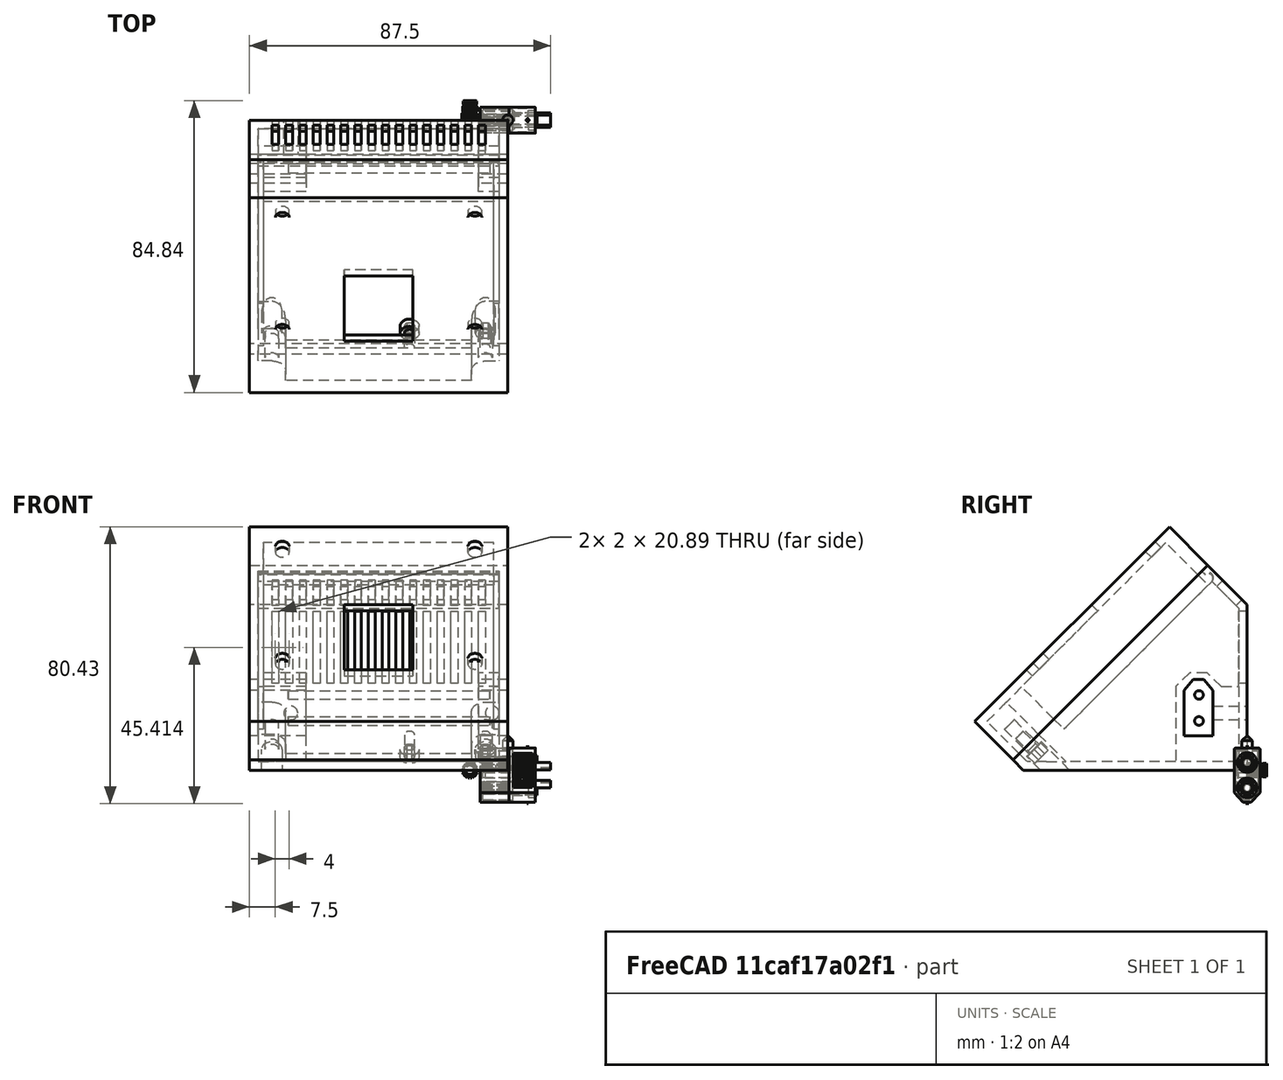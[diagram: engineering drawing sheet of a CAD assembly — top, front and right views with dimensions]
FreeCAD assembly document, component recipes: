
FREECAD ASSEMBLY — COMPONENT RECIPES ("moduleLidl_001_surBase35mm_009.1")

This assembly document has 8 components, labeled P0..P7 below (a component is one placed body or linked part). 4 of them carry a construction recipe — the FreeCAD feature program that regenerates the part from scratch, quoted from this document or its linked companion documents; the rest are supplied as boundary geometry only. No exploded tour is included for this assembly.
COMPONENT P0 — geometry summary ("adapt"; no construction recipe available for this part):
  bounding box: 65.0 x 49.5 x 49.5 mm
  tessellated surface: 2,488 triangles
  volume: 18576 mm^3 (12% of its bounding box)
  symmetry: mirror-symmetric across its x mid-plane
COMPONENT P1 — geometry summary ("fuse"; no construction recipe available for this part):
  bounding box: 31.7 x 29.8 x 15.0 mm
  tessellated surface: 6,264 triangles
  volume: 2885 mm^3 (20% of its bounding box)
  symmetry: mirror-symmetric across its x mid-plane
COMPONENT P2 — recipe-attached ("tigeLaiton001", modeled in this document).
Construction recipe (the document's own serialized feature program — sketch geometry with constraints, then the solid features built on it; lengths are millimeters unless a unit is written):

FEATURE [PartDesign::Plane] DatumPlane012  label="planBaseTige"
  AttachmentOffset = pos=(0,0,-5.18) rot=(0,0,1;0rad)
  Length = 60
  MapMode = 5
  Placement = pos=(-5.18,1.2e-15,-1.2e-15) rot=(0.57735,0.57735,0.57735;2.0944rad)
  ResizeMode = 0
  Support = -> [YZ_Plane012]
  Width = 60
  expr: .AttachmentOffset.Base.z = -<<tige>>.planBaseTigeposX
FEATURE [Sketcher::SketchObject] Sketch032  label="sk_tiges"
  FullyConstrained = true
  MapMode = 5
  Placement = pos=(-5.18,1.2e-15,-1.2e-15) rot=(0.57735,0.57735,0.57735;2.0944rad)
  Support = -> [DatumPlane012]
  expr: Constraints[0] = <<tige>>.tigeDiam
  expr: Constraints[1] = <<tige>>.tigePosY
  expr: Constraints[2] = <<tige>>.tigePosX
  sketch-geometry (1):
    g0: Circle CenterX=-14 CenterY=14.3 CenterZ=0 NormalX=0 NormalY=0 NormalZ=1 AngleXU=0 Radius=1.25
  constraints (3):
    c: Diameter(g0) = 2.5
    c: DistanceY(g-1,g0) = 14.3
    c: DistanceX(g0,g-1) = 14
FEATURE [PartDesign::Pad] Pad017  label="tigeBasse"
  AllowMultiFace = false
  Direction = (1,-1e-16,1e-16)
  Length = 58.62
  Length2 = 100
  Placement = pos=(-5.18,1e-15,-1e-15) rot=(0.57735,0.57735,0.57735;2.0944rad)
  Profile = -> Sketch032
  Reversed = true
  Type = 0
  expr: Length = <<tige>>.tigeLong
FEATURE [PartDesign::Body] Body007  label="tigeLaiton"
  Group = -> [DatumPlane012,Sketch032,Pad017]
  Origin = -> Origin016
  Tip = -> Pad017
FEATURE [PartDesign::Plane] DatumPlane013  label="planTige2"
  AttachmentOffset = pos=(0,0,-5.18) rot=(0,0,1;0rad)
  Length = 60
  MapMode = 5
  Placement = pos=(-5.18,1.2e-15,-1.2e-15) rot=(0.57735,0.57735,0.57735;2.0944rad)
  ResizeMode = 0
  Support = -> [YZ_Plane014]
  Width = 60
  expr: .AttachmentOffset.Base.z = -<<tige>>.planBaseTigeposX
FEATURE [Sketcher::SketchObject] Sketch033  label="sk_tige2"
  FullyConstrained = true
  MapMode = 5
  Placement = pos=(-5.18,1.2e-15,-1.2e-15) rot=(0.57735,0.57735,0.57735;2.0944rad)
  Support = -> [DatumPlane013]
  expr: Constraints[0] = <<tige>>.tigeDiam
  expr: Constraints[1] = <<tige>>.tigePosX
  expr: Constraints[2] = <<tige>>.tigePosY + <<tige>>.xtEcartBroches
  sketch-geometry (1):
    g0: Circle CenterX=-14 CenterY=21.86 CenterZ=0 NormalX=0 NormalY=0 NormalZ=1 AngleXU=0 Radius=1.25
  constraints (3):
    c: Diameter(g0) = 2.5
    c: DistanceX(g0,g-1) = 14
    c: DistanceY(g-1,g0) = 21.86
FEATURE [PartDesign::Pad] Pad018
  AllowMultiFace = false
  Direction = (1,-1e-16,1e-16)
  Length = 58.62
  Length2 = 100
  Placement = pos=(-5.18,1e-15,-1e-15) rot=(0.57735,0.57735,0.57735;2.0944rad)
  Profile = -> Sketch033
  Reversed = true
  Type = 0
  expr: Length = <<tige>>.tigeLong
FEATURE [PartDesign::Body] Body008  label="tige2"
  Group = -> [DatumPlane013,Sketch033,Pad018]
  Origin = -> Origin018
  Tip = -> Pad018
COMPONENT P3 — geometry summary ("xtVisInsertFix"; no construction recipe available for this part):
  bounding box: 20.2 x 17.7 x 16.6 mm
  tessellated surface: 21,322 triangles
  volume: 1306 mm^3 (22% of its bounding box)
COMPONENT P4 — recipe-attached ("visInsertFavFix", modeled in this document).
Construction recipe (the document's own serialized feature program — sketch geometry with constraints, then the solid features built on it; lengths are millimeters unless a unit is written):

FEATURE [Sketcher::SketchObject] Sketch034  label="Sketch"
  FullyConstrained = false
  MapMode = 5
  Support = -> [XY_Plane015]
  sketch-geometry (1):
    g0: Circle CenterX=0 CenterY=0 CenterZ=0 NormalX=0 NormalY=0 NormalZ=1 AngleXU=0 Radius=2.75
  constraints (2):
    c: Coincident(g0,g-1)
    c: Diameter(g0) = 5.5
FEATURE [PartDesign::Pad] Pad019  label="tete"
  AllowMultiFace = false
  Direction = (1,1,1)
  Length = 3
  Length2 = 100
  Profile = -> Sketch034
  Type = 0
FEATURE [Sketcher::SketchObject] Sketch001
  FullyConstrained = false
  MapMode = 5
  Placement = pos=(0,0,0) rot=(1,0,0;3.14159rad)
  Support = -> [Pad019]
  sketch-geometry (1):
    g0: Circle CenterX=0 CenterY=0 CenterZ=0 NormalX=0 NormalY=0 NormalZ=1 AngleXU=0 Radius=1.5
  constraints (2):
    c: Coincident(g0,g-1)
    c: Diameter(g0) = 3
FEATURE [PartDesign::Pad] Pad020  label="corps"
  AllowMultiFace = false
  BaseFeature = -> Pad019
  Direction = (1,1,1)
  Length = 6
  Length2 = 100
  Profile = -> Sketch001
  Type = 0
FEATURE [PartDesign::Plane] DatumPlane014
  AttachmentOffset = pos=(0,0,3) rot=(0,0,1;0rad)
  Length = 60
  MapMode = 5
  Placement = pos=(0,0,3) rot=(0,0,1;0rad)
  ResizeMode = 0
  Support = -> [XY_Plane015]
  Width = 60
FEATURE [Sketcher::SketchObject] Sketch035  label="Sketch002"
  FullyConstrained = false
  MapMode = 5
  Placement = pos=(0,0,3) rot=(0,0,1;0rad)
  Support = -> [DatumPlane014]
  sketch-geometry (7):
    g0: LineSegment StartX=0.721688 StartY=-1.25 StartZ=0 EndX=1.44338 EndY=1.0119e-12 EndZ=0
    g1: LineSegment StartX=1.44338 StartY=1.0119e-12 StartZ=0 EndX=0.721688 EndY=1.25 EndZ=0
    g2: LineSegment StartX=0.721688 StartY=1.25 StartZ=0 EndX=-0.721688 EndY=1.25 EndZ=0
    g3: LineSegment StartX=-0.721688 StartY=1.25 StartZ=0 EndX=-1.44338 EndY=8.689e-13 EndZ=0
    g4: LineSegment StartX=-1.44338 StartY=8.689e-13 StartZ=0 EndX=-0.721688 EndY=-1.25 EndZ=0
    g5: LineSegment StartX=-0.721688 StartY=-1.25 StartZ=0 EndX=0.721688 EndY=-1.25 EndZ=0
    g6: Circle CenterX=0 CenterY=0 CenterZ=0 NormalX=0 NormalY=0 NormalZ=1 AngleXU=0 Radius=1.44338
  constraints (16):
    c: Coincident(g0,g1)
    c: Coincident(g1,g2)
    c: Coincident(g2,g3)
    c: Coincident(g3,g4)
    c: Coincident(g4,g5)
    c: Coincident(g5,g0)
    c: Equal(g0, g1-g5) x5
    c: PointOnObject(g0,g6)
    c: PointOnObject(g1,g6)
    c: PointOnObject(g2,g6)
    c: PointOnObject(g3,g6)
    c: PointOnObject(g4,g6)
    c: PointOnObject(g5,g6)
    c: Coincident(g6,g-1)
    c: Horizontal(g2)
    c: DistanceY(g0,g1) = 2.5
FEATURE [PartDesign::Pocket] Pocket016  label="emprunte"
  AllowMultiFace = false
  BaseFeature = -> Pad020
  Direction = (1,1,1)
  Length = 4
  Length2 = 100
  Profile = -> Sketch035
  Type = 0
FEATURE [PartDesign::Body] Body009  label="visTHCM3x6_FAV001"
  Group = -> [Sketch034,Pad019,Sketch001,Pad020,DatumPlane014,Sketch035,Pocket016]
  Origin = -> Origin019
  Placement = pos=(-6.5,-61.8718,6.01041) rot=(1,0,0;3.92699rad)
  Tip = -> Pocket016
COMPONENT P5 — recipe-attached ("visInserFavMob", modeled in this document).
Construction recipe (the document's own serialized feature program — sketch geometry with constraints, then the solid features built on it; lengths are millimeters unless a unit is written):

FEATURE [Sketcher::SketchObject] Sketch036
  FullyConstrained = false
  MapMode = 5
  Support = -> [XY_Plane016]
  sketch-geometry (1):
    g0: Circle CenterX=0 CenterY=0 CenterZ=0 NormalX=0 NormalY=0 NormalZ=1 AngleXU=0 Radius=2.75
  constraints (2):
    c: Coincident(g0,g-1)
    c: Diameter(g0) = 5.5
FEATURE [PartDesign::Pad] Pad021  label="tete001"
  AllowMultiFace = false
  Direction = (1,1,1)
  Length = 3
  Length2 = 100
  Profile = -> Sketch036
  Type = 0
FEATURE [Sketcher::SketchObject] Sketch037
  FullyConstrained = false
  MapMode = 5
  Placement = pos=(0,0,0) rot=(1,0,0;3.14159rad)
  Support = -> [Pad021]
  sketch-geometry (1):
    g0: Circle CenterX=0 CenterY=0 CenterZ=0 NormalX=0 NormalY=0 NormalZ=1 AngleXU=0 Radius=1.5
  constraints (2):
    c: Coincident(g0,g-1)
    c: Diameter(g0) = 3
FEATURE [PartDesign::Pad] Pad022  label="corps001"
  AllowMultiFace = false
  BaseFeature = -> Pad021
  Direction = (1,1,1)
  Length = 6
  Length2 = 100
  Profile = -> Sketch037
  Type = 0
FEATURE [PartDesign::Plane] DatumPlane015
  AttachmentOffset = pos=(0,0,3) rot=(0,0,1;0rad)
  Length = 60
  MapMode = 5
  Placement = pos=(0,0,3) rot=(0,0,1;0rad)
  ResizeMode = 0
  Support = -> [XY_Plane016]
  Width = 60
FEATURE [Sketcher::SketchObject] Sketch038
  FullyConstrained = false
  MapMode = 5
  Placement = pos=(0,0,3) rot=(0,0,1;0rad)
  Support = -> [DatumPlane015]
  sketch-geometry (7):
    g0: LineSegment StartX=0.721688 StartY=-1.25 StartZ=0 EndX=1.44338 EndY=1.0119e-12 EndZ=0
    g1: LineSegment StartX=1.44338 StartY=1.0119e-12 StartZ=0 EndX=0.721688 EndY=1.25 EndZ=0
    g2: LineSegment StartX=0.721688 StartY=1.25 StartZ=0 EndX=-0.721688 EndY=1.25 EndZ=0
    g3: LineSegment StartX=-0.721688 StartY=1.25 StartZ=0 EndX=-1.44338 EndY=8.689e-13 EndZ=0
    g4: LineSegment StartX=-1.44338 StartY=8.689e-13 StartZ=0 EndX=-0.721688 EndY=-1.25 EndZ=0
    g5: LineSegment StartX=-0.721688 StartY=-1.25 StartZ=0 EndX=0.721688 EndY=-1.25 EndZ=0
    g6: Circle CenterX=0 CenterY=0 CenterZ=0 NormalX=0 NormalY=0 NormalZ=1 AngleXU=0 Radius=1.44338
  constraints (16):
    c: Coincident(g0,g1)
    c: Coincident(g1,g2)
    c: Coincident(g2,g3)
    c: Coincident(g3,g4)
    c: Coincident(g4,g5)
    c: Coincident(g5,g0)
    c: Equal(g0, g1-g5) x5
    c: PointOnObject(g0,g6)
    c: PointOnObject(g1,g6)
    c: PointOnObject(g2,g6)
    c: PointOnObject(g3,g6)
    c: PointOnObject(g4,g6)
    c: PointOnObject(g5,g6)
    c: Coincident(g6,g-1)
    c: Horizontal(g2)
    c: DistanceY(g0,g1) = 2.5
FEATURE [PartDesign::Pocket] Pocket017  label="emprunte001"
  AllowMultiFace = false
  BaseFeature = -> Pad022
  Direction = (1,1,1)
  Length = 4
  Length2 = 100
  Profile = -> Sketch038
  Type = 0
FEATURE [PartDesign::Body] Body010  label="visTHCM3x6_FAV002"
  Group = -> [Sketch036,Pad021,Sketch037,Pad022,DatumPlane015,Sketch038,Pocket017]
  Origin = -> Origin020
  Placement = pos=(-28.5,-61.8718,6.01041) rot=(1,0,0;3.92699rad)
  Tip = -> Pocket017
COMPONENT P6 — recipe-attached ("BaseModule", modeled in this document).
Construction recipe (the document's own serialized feature program — sketch geometry with constraints, then the solid features built on it; lengths are millimeters unless a unit is written):

FEATURE [PartDesign::FeatureBase] Clone
  BaseFeature = -> Slice_child0
FEATURE [PartDesign::FeatureBase] Clone001
  BaseFeature = -> Slice_child1
FEATURE [PartDesign::Thickness] Thickness
  Base = -> Clone [Face7]
  BaseFeature = -> Clone
  Intersection = false
  Join = 0
  Mode = 0
  Reversed = true
  SupportTransform = false
  Value = 2.5
  expr: Value = <<sp>>.epaisseurParois
FEATURE [PartDesign::Thickness] Thickness001
  Base = -> Clone001 [Face5]
  BaseFeature = -> Clone001
  Intersection = false
  Join = 0
  Mode = 0
  Reversed = true
  SupportTransform = false
  Value = 2.5
  expr: Value = <<sp>>.epaisseurParois
FEATURE [PartDesign::Plane] DatumPlane001  label="planXt"
  AttachmentOffset = pos=(0,0,-2.5) rot=(0,0,1;0rad)
  Length = 110.737
  MapMode = 5
  Placement = pos=(-2.5,6e-16,-6e-16) rot=(0.57735,0.57735,0.57735;2.0944rad)
  ResizeMode = 0
  Support = -> [YZ_Plane002]
  Width = 102.305
  expr: .AttachmentOffset.Base.z = -<<sp>>.epaisseurParois
FEATURE [Sketcher::SketchObject] Sketch002  label="sk_renfortXt"
  FullyConstrained = true
  MapMode = 5
  Placement = pos=(-2.5,6e-16,-6e-16) rot=(0.57735,0.57735,0.57735;2.0944rad)
  Support = -> [DatumPlane001]
  expr: .Constraints.dist = <<sp>>.xt60distanceAngleBord
  expr: .Constraints.epRf = <<sp>>.xt60epRenfort
  expr: Constraints[13] = <<sp>>.xt60largeurFetiere
  expr: Constraints[14] = <<sp>>.xt60hauteur
  expr: Constraints[15] = <<sp>>.xt60hauteurToit
  expr: Constraints[16] = <<sp>>.xt60base
  expr: Constraints[18] = .Constraints.dist
  expr: Constraints[31] = <<sp>>.epaisseurParois
  expr: Constraints[32] = .Constraints.epRf
  expr: Constraints[34] = .Constraints.epRf
  expr: Constraints[45] = <<sp>>.epaisseurParois
  sketch-geometry (17):
    g0: LineSegment StartX=-18.3 StartY=10 StartZ=0 EndX=-18.3 EndY=23.25 EndZ=0
    g1: LineSegment StartX=-18.3 StartY=23.25 StartZ=0 EndX=-15.65 EndY=25.75 EndZ=0
    g2: LineSegment StartX=-15.65 StartY=25.75 StartZ=0 EndX=-12.65 EndY=25.75 EndZ=0
    g3: LineSegment StartX=-12.65 StartY=25.75 StartZ=0 EndX=-10 EndY=23.25 EndZ=0
    g4: LineSegment StartX=-10 StartY=23.25 StartZ=0 EndX=-10 EndY=10 EndZ=0
    g5: LineSegment StartX=-10 StartY=10 StartZ=0 EndX=-18.3 EndY=10 EndZ=0
    g6: LineSegment StartX=-14.15 StartY=10 StartZ=0 EndX=-14.15 EndY=25.75 EndZ=0
    g7: LineSegment StartX=-16.6431 StartY=28.25 StartZ=0 EndX=-20.8 EndY=24.3284 EndZ=0
    g8: LineSegment StartX=-20.8 StartY=24.3284 StartZ=0 EndX=-20.8 EndY=2.5 EndZ=0
    g9: LineSegment StartX=-20.8 StartY=2.5 StartZ=0 EndX=-7.5 EndY=2.5 EndZ=0
    g10: LineSegment StartX=-7.5 StartY=2.5 StartZ=0 EndX=-7.5 EndY=24.3284 EndZ=0
    g11: LineSegment StartX=-7.5 StartY=24.3284 StartZ=0 EndX=-11.6569 EndY=28.25 EndZ=0
    g12: LineSegment StartX=-11.6569 StartY=28.25 StartZ=0 EndX=-16.6431 EndY=28.25 EndZ=0
    g13: LineSegment StartX=-7.5 StartY=24.3284 StartZ=0 EndX=-2.5 EndY=24.3284 EndZ=0
    g14: LineSegment StartX=-2.5 StartY=24.3284 StartZ=0 EndX=-2.5 EndY=2.5 EndZ=0
    g15: LineSegment StartX=-2.5 StartY=2.5 StartZ=0 EndX=-7.5 EndY=2.5 EndZ=0
    g16: LineSegment StartX=-7.5 StartY=2.5 StartZ=0 EndX=-7.5 EndY=24.3284 EndZ=0
  constraints (46):
    c: Vertical(g0)
    c: Coincident(g0,g1)
    c: Coincident(g1,g2)
    c: Horizontal(g2)
    c: Coincident(g2,g3)
    c: Coincident(g3,g4)
    c: Vertical(g4)
    c: Coincident(g4,g5)
    c: Coincident(g5,g0)
    c: Horizontal(g5)
    c: Symmetric(g1,g2,g6)
    c: Equal(g0,g4)
    c: Symmetric(g0,g4,g6)
    c: DistanceX(g2,g2) = 3
    c: DistanceY(g4,g4) = 13.25
    c: DistanceY(g3,g2) = 2.5
    c: DistanceX(g5,g5) = 8.3
    c: DistanceX(g4,g-1) = 10  'dist'
    c: DistanceY(g-1,g4) = 10
    c: Coincident(g7,g8)
    c: Vertical(g8)
    c: Coincident(g8,g9)
    c: Horizontal(g9)
    c: Coincident(g9,g10)
    c: Coincident(g10,g11)
    c: Coincident(g11,g12)
    c: Coincident(g12,g7)
    c: Symmetric(g7,g10,g6)
    c: Symmetric(g7,g11,g6)
    c: Symmetric(g8,g9,g6)
    c: DistanceX(g8,g0) = 2.5  'epRf'
    c: DistanceY(g-1,g9) = 2.5
    c: Distance(g7,g1) = 2.5
    c: Parallel(g1,g7)
    c: DistanceY(g2,g11) = 2.5
    c: Coincident(g13,g14)
    c: Coincident(g14,g15)
    c: Coincident(g15,g16)
    c: Coincident(g16,g13)
    c: Horizontal(g13)
    c: Horizontal(g15)
    c: Vertical(g14)
    c: Vertical(g16)
    c: Coincident(g13,g11)
    c: Horizontal(g14,g9)
    c: DistanceX(g14,g-1) = 2.5
FEATURE [PartDesign::Pad] Pad001  label="renfortXt"
  AllowMultiFace = false
  BaseFeature = -> Thickness
  Direction = (1,-1e-16,1e-16)
  Length = 70
  Length2 = 100
  Profile = -> Sketch002
  Reversed = true
  Type = 0
  expr: Length = <<sp>>.largeurModuleBase - 2 * <<sp>>.epaisseurParois
FEATURE [Sketcher::SketchObject] Sketch003  label="sk_trouXt"
  FullyConstrained = true
  MapMode = 5
  Placement = pos=(0,0,0) rot=(0.57735,0.57735,0.57735;2.0944rad)
  Support = -> [YZ_Plane002]
  expr: .Constraints.dist = <<sp>>.xt60distanceAngleBord
  expr: Constraints[13] = <<sp>>.xt60base
  expr: Constraints[14] = <<sp>>.xt60hauteur
  expr: Constraints[15] = <<sp>>.xt60hauteurToit + <<sp>>.xtJeu
  expr: Constraints[16] = <<sp>>.xt60largeurFetiere
  expr: Constraints[18] = .Constraints.dist
  sketch-geometry (7):
    g0: LineSegment StartX=-18.3 StartY=10 StartZ=0 EndX=-18.3 EndY=23.25 EndZ=0
    g1: LineSegment StartX=-18.3 StartY=23.25 StartZ=0 EndX=-15.65 EndY=26.35 EndZ=0
    g2: LineSegment StartX=-15.65 StartY=26.35 StartZ=0 EndX=-12.65 EndY=26.35 EndZ=0
    g3: LineSegment StartX=-12.65 StartY=26.35 StartZ=0 EndX=-10 EndY=23.25 EndZ=0
    g4: LineSegment StartX=-10 StartY=23.25 StartZ=0 EndX=-10 EndY=10 EndZ=0
    g5: LineSegment StartX=-10 StartY=10 StartZ=0 EndX=-18.3 EndY=10 EndZ=0
    g6: LineSegment StartX=-14.15 StartY=10 StartZ=0 EndX=-14.15 EndY=26.35 EndZ=0
  constraints (19):
    c: Vertical(g0)
    c: Coincident(g0,g1)
    c: Coincident(g1,g2)
    c: Horizontal(g2)
    c: Coincident(g2,g3)
    c: Coincident(g3,g4)
    c: Coincident(g4,g5)
    c: Coincident(g5,g0)
    c: Horizontal(g5)
    c: Symmetric(g1,g2,g6)
    c: Symmetric(g0,g3,g6)
    c: Vertical(g6)
    c: Symmetric(g0,g4,g6)
    c: DistanceX(g5,g5) = 8.3
    c: DistanceY(g4,g4) = 13.25
    c: DistanceY(g3,g2) = 3.1
    c: DistanceX(g2,g2) = 3
    c: DistanceX(g4,g-1) = 10  'dist'
    c: DistanceY(g-1,g4) = 10
FEATURE [PartDesign::Pocket] Pocket
  AllowMultiFace = false
  BaseFeature = -> Pad001
  Direction = (-1,2e-16,-3e-16)
  Length = 75
  Length2 = 100
  Profile = -> Sketch003
  Type = 0
  expr: Length = <<sp>>.largeurModuleBase
FEATURE [PartDesign::Plane] DatumPlane002  label="planDecoupeRenfortXt"
  AttachmentOffset = pos=(0,0,2.5) rot=(0,0,1;0rad)
  Length = 118.392
  MapMode = 5
  Placement = pos=(0,-2.5,-6e-16) rot=(1,0,0;1.5708rad)
  ResizeMode = 0
  Support = -> [XZ_Plane002]
  Width = 102.961
  expr: .AttachmentOffset.Base.z = <<sp>>.epaisseurParois
FEATURE [Sketcher::SketchObject] Sketch004  label="sk_decoupRenfXt"
  FullyConstrained = true
  MapMode = 5
  Placement = pos=(0,-2.5,-6e-16) rot=(1,0,0;1.5708rad)
  Support = -> [DatumPlane002]
  expr: Constraints[10] = <<sp>>.xt60LongueurRenfortPetit + <<sp>>.epaisseurParois
  expr: Constraints[11] = <<sp>>.largeurModuleBase - (<<sp>>.xt60longueurRenfortGrand + <<sp>>.epaisseurParois)
  expr: Constraints[8] = <<sp>>.epaisseurParois
  expr: Constraints[9] = <<sp>>.xt60distanceAngleBord + <<sp>>.xt60hauteur + <<sp>>.xt60hauteurToit + <<sp>>.xt60epRenfort
  sketch-geometry (4):
    g0: LineSegment StartX=-58.5 StartY=28.25 StartZ=0 EndX=-8.5 EndY=28.25 EndZ=0
    g1: LineSegment StartX=-8.5 StartY=28.25 StartZ=0 EndX=-8.5 EndY=2.5 EndZ=0
    g2: LineSegment StartX=-8.5 StartY=2.5 StartZ=0 EndX=-58.5 EndY=2.5 EndZ=0
    g3: LineSegment StartX=-58.5 StartY=2.5 StartZ=0 EndX=-58.5 EndY=28.25 EndZ=0
  constraints (12):
    c: Coincident(g0,g1)
    c: Coincident(g1,g2)
    c: Coincident(g2,g3)
    c: Coincident(g3,g0)
    c: Horizontal(g0)
    c: Horizontal(g2)
    c: Vertical(g1)
    c: Vertical(g3)
    c: DistanceY(g-1,g1) = 2.5
    c: DistanceY(g-1,g0) = 28.25
    c: DistanceX(g1,g-1) = 8.5
    c: DistanceX(g2,g-1) = 58.5
FEATURE [PartDesign::Pocket] Pocket001  label="decoupeRenfXt"
  AllowMultiFace = false
  BaseFeature = -> Pocket
  Direction = (0,1,2e-16)
  Length = 23.3
  Length2 = 100
  Profile = -> Sketch004
  Reversed = true
  Type = 0
  expr: Length = <<sp>>.xt60distanceAngleBord + <<sp>>.xt60base + 2 * <<sp>>.xt60epRenfort
FEATURE [Sketcher::SketchObject] Sketch005  label="xt60PercagePostMale"
  FullyConstrained = true
  MapMode = 5
  Placement = pos=(0,0,0) rot=(1,0,0;1.5708rad)
  Support = -> [XZ_Plane002]
  expr: Constraints[0] = <<sp>>.insertDiamPercage
  expr: Constraints[1] = <<sp>>.insertDistanceTrouBordMale
  expr: Constraints[2] = <<sp>>.insertHauteur
  sketch-geometry (1):
    g0: Circle CenterX=-4.5 CenterY=16.625 CenterZ=0 NormalX=0 NormalY=0 NormalZ=1 AngleXU=0 Radius=2
  constraints (3):
    c: Diameter(g0) = 4
    c: DistanceX(g0,g-1) = 4.5
    c: DistanceY(g-1,g0) = 16.625
FEATURE [PartDesign::Pocket] Pocket002  label="insertXtMale"
  AllowMultiFace = false
  BaseFeature = -> Pocket001
  Direction = (0,1,2e-16)
  Length = 10
  Length2 = 100
  Profile = -> Sketch005
  Reversed = true
  Type = 0
  expr: Length = <<sp>>.insertProfondeurPercage
FEATURE [Sketcher::SketchObject] Sketch006  label="xt60PercagePostFem"
  FullyConstrained = true
  MapMode = 5
  Placement = pos=(0,0,0) rot=(1,0,0;1.5708rad)
  Support = -> [XZ_Plane002]
  expr: Constraints[0] = <<sp>>.insertDiamPercage
  expr: Constraints[1] = <<sp>>.insertDistanceTrouBordFem
  expr: Constraints[2] = <<sp>>.insertHauteur
  sketch-geometry (1):
    g0: Circle CenterX=-63 CenterY=16.625 CenterZ=0 NormalX=0 NormalY=0 NormalZ=1 AngleXU=0 Radius=2
  constraints (3):
    c: Diameter(g0) = 4
    c: DistanceX(g0,g-1) = 63
    c: DistanceY(g-1,g0) = 16.625
FEATURE [PartDesign::Pocket] Pocket003  label="insertXt60Fem"
  AllowMultiFace = false
  BaseFeature = -> Pocket002
  Direction = (0,1,2e-16)
  Length = 10
  Length2 = 100
  Profile = -> Sketch006
  Reversed = true
  Type = 0
  expr: Length = <<sp>>.insertProfondeurPercage
FEATURE [PartDesign::Plane] DatumPlane003
  AttachmentOffset = pos=(0,0,2.5) rot=(0,0,1;0rad)
  Length = 119.287
  MapMode = 2
  Placement = pos=(0,0,2.5) rot=(0,0,1;0rad)
  ResizeMode = 0
  Support = -> [XY_Plane002]
  Width = 112.287
  expr: .AttachmentOffset.Base.z = <<sp>>.epaisseurParois
FEATURE [PartDesign::Plane] DatumPlane004  label="planTrancheur"
  AttachmentOffset = pos=(0,0,71) rot=(-1,0,0;0.785398rad)
  Length = 122.411
  MapMode = 5
  Placement = pos=(0,-71,-1.58e-14) rot=(1,0,0;0.785398rad)
  ResizeMode = 0
  Support = -> [XZ_Plane002]
  Width = 147.971
  expr: .AttachmentOffset.Base.z = <<sp>>.planTrancheur
FEATURE [Sketcher::SketchObject] Sketch008
  FullyConstrained = true
  MapMode = 5
  Placement = pos=(0,-71,-2.13e-14) rot=(1,0,0;0.785398rad)
  Support = -> [DatumPlane004]
  expr: .Constraints.dist = <<sp>>.epaisseurParois
  expr: Constraints[13] = <<sp>>.epaisseurParois
  expr: Constraints[16] = <<sp>>.insertDiamPercage / 2 + <<sp>>.insertFAVMargeDist
  expr: Constraints[1] = <<sp>>.insertFavDistAuZeroDuPLan
  expr: Constraints[21] = <<sp>>.insertFAVDistBord
  expr: Constraints[22] = <<sp>>.largeurModuleBase - <<sp>>.epaisseurParois
  sketch-geometry (7):
    g0: LineSegment StartX=-2.5 StartY=4.24264 StartZ=0 EndX=-72.5 EndY=4.24264 EndZ=0
    g1: LineSegment StartX=-6.5 StartY=14.7426 StartZ=0 EndX=-2.5 EndY=14.7426 EndZ=0
    g2: LineSegment StartX=-2.5 StartY=14.7426 StartZ=0 EndX=-2.5 EndY=6.74264 EndZ=0
    g3: LineSegment StartX=-2.5 StartY=6.74264 StartZ=0 EndX=-10.5 EndY=6.74264 EndZ=0
    g4: LineSegment StartX=-10.5 StartY=6.74264 StartZ=0 EndX=-10.5 EndY=10.7426 EndZ=0
    g5: ArcOfCircle CenterX=-6.5 CenterY=10.7426 CenterZ=0 NormalX=0 NormalY=0 NormalZ=1 AngleXU=0 Radius=4 StartAngle=1.5708 EndAngle=3.14159
    g6: LineSegment StartX=-6.5 StartY=10.7426 StartZ=0 EndX=-6.5 EndY=6.74264 EndZ=0
  constraints (23):
    c: Horizontal(g0)
    c: DistanceY(g-1,g0) = 4.24264
    c: DistanceX(g0,g-1) = 2.5  'dist'
    c: Horizontal(g1)
    c: Coincident(g1,g2)
    c: Vertical(g2)
    c: Coincident(g2,g3)
    c: Horizontal(g3)
    c: Coincident(g3,g4)
    c: Vertical(g4)
    c: Vertical(g2,g0)
    c: Equal(g3,g2)
    c: Equal(g4,g1)
    c: DistanceY(g0,g2) = 2.5
    c: Coincident(g5,g4)
    c: Coincident(g5,g1)
    c: DistanceX(g5,g2) = 4
    c: Coincident(g6,g5)
    c: PointOnObject(g6,g3)
    c: Vertical(g6)
    c: Vertical(g5,g1)
    c: DistanceX(g3,g3) = 8
    c: DistanceX(g0,g-1) = 72.5
FEATURE [PartDesign::Pad] Pad003  label="padTrouFAVDroite"
  AllowMultiFace = false
  BaseFeature = -> Pocket003
  Direction = (0,-0.707107,0.707107)
  Length = 10
  Length2 = 100
  Profile = -> Sketch008
  Reversed = true
  Type = 3
  UpToFace = -> DatumPlane003
FEATURE [Sketcher::SketchObject] Sketch009
  FullyConstrained = true
  MapMode = 5
  Placement = pos=(0,-71,-2.13e-14) rot=(1,0,0;0.785398rad)
  Support = -> [DatumPlane004]
  expr: .Constraints.larg = <<sp>>.insertFAVDistBord
  expr: Constraints[11] = .Constraints.larg / 2
  expr: Constraints[12] = <<sp>>.largeurModuleBase
  expr: Constraints[13] = <<sp>>.insertFavDistAuZeroDuPLan
  expr: Constraints[14] = <<sp>>.epaisseurParois
  expr: Constraints[15] = <<sp>>.epaisseurParois
  expr: Constraints[8] = .Constraints.larg
  sketch-geometry (6):
    g0: LineSegment StartX=-72.5 StartY=6.74264 StartZ=0 EndX=-64.5 EndY=6.74264 EndZ=0
    g1: LineSegment StartX=-64.5 StartY=6.74264 StartZ=0 EndX=-64.5 EndY=10.7426 EndZ=0
    g2: LineSegment StartX=-68.5 StartY=14.7426 StartZ=0 EndX=-72.5 EndY=14.7426 EndZ=0
    g3: LineSegment StartX=-72.5 StartY=14.7426 StartZ=0 EndX=-72.5 EndY=6.74264 EndZ=0
    g4: ArcOfCircle CenterX=-68.5 CenterY=10.7426 CenterZ=0 NormalX=0 NormalY=0 NormalZ=1 AngleXU=0 Radius=4 StartAngle=0 EndAngle=1.5708
    g5: GeomPoint X=-75 Y=4.24264 Z=0
  constraints (16):
    c: Coincident(g0,g1)
    c: Coincident(g2,g3)
    c: Coincident(g3,g0)
    c: Horizontal(g0)
    c: Horizontal(g2)
    c: Vertical(g1)
    c: Vertical(g3)
    c: DistanceX(g0,g0) = 8  'larg'
    c: DistanceY(g3,g3) = 8
    c: Tangent(g2,g4) = -1.5708
    c: Tangent(g1,g4) = -1.5708
    c: DistanceX(g0,g4) = 4
    c: DistanceX(g5,g-1) = 75
    c: DistanceY(g-1,g5) = 4.24264
    c: DistanceX(g5,g0) = 2.5
    c: DistanceY(g5,g0) = 2.5
FEATURE [PartDesign::Pad] Pad004  label="padTrouFavGauche"
  AllowMultiFace = false
  BaseFeature = -> Pad003
  Direction = (0,-0.707107,0.707107)
  Length = 10
  Length2 = 100
  Profile = -> Sketch009
  Type = 3
  UpToFace = -> DatumPlane003 [Plane]
FEATURE [Sketcher::SketchObject] Sketch010
  FullyConstrained = true
  MapMode = 5
  Placement = pos=(0,-71,-2.13e-14) rot=(1,0,0;0.785398rad)
  Support = -> [DatumPlane004]
  expr: Constraints[0] = <<sp>>.insertFAVDistBord / 2 + <<sp>>.epaisseurParois
  expr: Constraints[1] = <<sp>>.insertFavDistAuZeroDuPLan + <<sp>>.epaisseurParois + <<sp>>.insertFAVDistBord / 2
  expr: Constraints[2] = <<sp>>.insertDiamPercage
  sketch-geometry (1):
    g0: Circle CenterX=-6.5 CenterY=10.7426 CenterZ=0 NormalX=0 NormalY=0 NormalZ=1 AngleXU=0 Radius=2
  constraints (3):
    c: DistanceX(g0,g-1) = 6.5
    c: DistanceY(g-1,g0) = 10.7426
    c: Diameter(g0) = 4
FEATURE [PartDesign::Pocket] Pocket004  label="trouDroit"
  AllowMultiFace = false
  BaseFeature = -> Pad004
  Direction = (0,0.707107,-0.707107)
  Length = 5
  Length2 = 100
  Profile = -> Sketch010
  Type = 1
FEATURE [Sketcher::SketchObject] Sketch011
  FullyConstrained = true
  MapMode = 5
  Placement = pos=(0,-71,-2.13e-14) rot=(1,0,0;0.785398rad)
  Support = -> [DatumPlane004]
  expr: Constraints[0] = <<sp>>.insertDiamPercage
  expr: Constraints[1] = <<sp>>.largeurModuleBase - <<sp>>.epaisseurParois - <<sp>>.insertFAVDistBord / 2
  expr: Constraints[2] = <<sp>>.insertFavDistAuZeroDuPLan + <<sp>>.epaisseurParois + <<sp>>.insertFAVDistBord / 2
  sketch-geometry (1):
    g0: Circle CenterX=-68.5 CenterY=10.7426 CenterZ=0 NormalX=0 NormalY=0 NormalZ=1 AngleXU=0 Radius=2
  constraints (3):
    c: Diameter(g0) = 4
    c: DistanceX(g0,g-1) = 68.5
    c: DistanceY(g-1,g0) = 10.7426
FEATURE [PartDesign::Pocket] Pocket005  label="trouGauche"
  AllowMultiFace = false
  BaseFeature = -> Pocket004
  Direction = (0,0.707107,-0.707107)
  Length = 5
  Length2 = 100
  Profile = -> Sketch011
  Type = 1
FEATURE [PartDesign::Plane] DatumPlane005  label="planTeteVisFav"
  AttachmentOffset = pos=(0,0,68) rot=(-1,0,0;0.785398rad)
  Length = 122.411
  MapMode = 5
  Placement = pos=(0,-68,-1.51e-14) rot=(1,0,0;0.785398rad)
  ResizeMode = 0
  Support = -> [XZ_Plane002]
  Width = 147.971
  expr: .AttachmentOffset.Base.z = <<sp>>.planTrancheur - 3
FEATURE [Sketcher::SketchObject] Sketch012
  ExternalGeometry = -> [Pocket005]
  FullyConstrained = true
  MapMode = 5
  Placement = pos=(0,-68,-1.42e-14) rot=(1,0,0;0.785398rad)
  Support = -> [DatumPlane005]
  expr: Constraints[1] = <<sp>>.visM3DiamEncastrement
  sketch-geometry (2):
    g0: Circle CenterX=-6.5 CenterY=8.62132 CenterZ=0 NormalX=0 NormalY=0 NormalZ=1 AngleXU=0 Radius=3
    g1: Circle CenterX=-68.5 CenterY=8.62132 CenterZ=0 NormalX=0 NormalY=0 NormalZ=1 AngleXU=0 Radius=3
  constraints (4):
    c: Equal(g0,g1)
    c: Diameter(g1) = 6
    c: Coincident(g1,g-4)
    c: Coincident(g-3,g0)
FEATURE [PartDesign::Pocket] Pocket006  label="evidementTeteVisFav"
  AllowMultiFace = false
  BaseFeature = -> Pocket005
  Direction = (0,0.707107,-0.707107)
  Length = 20
  Length2 = 100
  Profile = -> Sketch012
  Type = 1
FEATURE [Sketcher::SketchObject] Sketch014
  FullyConstrained = true
  MapMode = 5
  Placement = pos=(0,0,0) rot=(1,0,0;1.5708rad)
  Support = -> [XZ_Plane002]
  expr: Constraints[12] = <<sp>>.xt60distanceAngleBord + <<sp>>.xt60hauteur + <<sp>>.ventilDistBordFente
  expr: Constraints[13] = <<sp>>.ventilLargeurFentes
  expr: Constraints[14] = <<sp>>.ventilEcartfente / 2
  expr: Constraints[15] = <<sp>>.hauteurDuDos - <<sp>>.ventilDistBordFente
  expr: Constraints[2] = <<sp>>.hauteurDuDos
  expr: Constraints[3] = <<sp>>.largeurModuleBase / 2
  sketch-geometry (5):
    g0: LineSegment StartX=-37.5 StartY=0 StartZ=0 EndX=-37.5 EndY=48.1371 EndZ=0
    g1: LineSegment StartX=-40.5 StartY=46.1371 StartZ=0 EndX=-38.5 EndY=46.1371 EndZ=0
    g2: LineSegment StartX=-38.5 StartY=46.1371 StartZ=0 EndX=-38.5 EndY=25.25 EndZ=0
    g3: LineSegment StartX=-38.5 StartY=25.25 StartZ=0 EndX=-40.5 EndY=25.25 EndZ=0
    g4: LineSegment StartX=-40.5 StartY=25.25 StartZ=0 EndX=-40.5 EndY=46.1371 EndZ=0
  constraints (16):
    c: PointOnObject(g0,g-1)
    c: Vertical(g0)
    c: DistanceY(g0,g0) = 48.1371
    c: DistanceX(g0,g-1) = 37.5
    c: Coincident(g1,g2)
    c: Coincident(g2,g3)
    c: Coincident(g3,g4)
    c: Coincident(g4,g1)
    c: Horizontal(g1)
    c: Horizontal(g3)
    c: Vertical(g2)
    c: Vertical(g4)
    c: DistanceY(g-1,g2) = 25.25
    c: DistanceX(g1,g1) = 2
    c: DistanceX(g2,g0) = 1
    c: DistanceY(g-1,g1) = 46.1371
FEATURE [PartDesign::Pocket] Pocket008  label="ventilFente1"
  AllowMultiFace = false
  BaseFeature = -> Pocket006
  Direction = (0,1,2e-16)
  Length = 2.5
  Length2 = 100
  Profile = -> Sketch014
  Reversed = true
  Type = 0
  expr: Length = <<sp>>.epaisseurParois
FEATURE [PartDesign::LinearPattern] LinearPattern  label="ventilDosRepeat1"
  BaseFeature = -> Pocket008
  Direction = -> Sketch014 [H_Axis]
  Length = 28
  Occurrences = 8
  Originals = -> [Pocket008]
  Reversed = true
  expr: Length = <<sp>>.ventilLargeurRepet
  expr: Occurrences = <<sp>>.ventilNbrFents
FEATURE [PartDesign::LinearPattern] LinearPattern001  label="ventilDosRepeat2"
  BaseFeature = -> LinearPattern
  Direction = -> Sketch014 [H_Axis]
  Length = 32
  Occurrences = 9
  Originals = -> [Pocket008]
  expr: Length = <<sp>>.ventilLargeurRepet + <<sp>>.ventilEcartfente + <<sp>>.ventilLargeurFentes
  expr: Occurrences = <<sp>>.ventilNbrFents + 1
FEATURE [PartDesign::Plane] DatumPlane006  label="planVentilSup"
  AttachmentOffset = pos=(0,0,-48.1371) rot=(1,0,0;0.785398rad)
  Length = 122.411
  MapMode = 5
  Placement = pos=(0,48.1371,1.07e-14) rot=(1,0,0;2.35619rad)
  ResizeMode = 0
  Support = -> [XZ_Plane002]
  Width = 147.971
  expr: .AttachmentOffset.Base.z = -<<sp>>.hauteurDuDos
FEATURE [Sketcher::SketchObject] Sketch015
  FullyConstrained = true
  MapMode = 5
  Placement = pos=(0,48.1371,1.07e-14) rot=(1,0,0;2.35619rad)
  Support = -> [DatumPlane006]
  expr: Constraints[10] = <<sp>>.ventilLargeurFentes
  expr: Constraints[11] = (<<sp>>.largeurModuleBase + <<sp>>.ventilEcartfente) / 2
  expr: Constraints[8] = <<sp>>.distanceAuZeroPlanBorArriere + <<sp>>.ventilDistBordFente
  expr: Constraints[9] = <<sp>>.longPetitRetSupSansFav - 2 * <<sp>>.ventilDistBordFente - <<sp>>.favBordureProf
  sketch-geometry (4):
    g0: LineSegment StartX=-38.5 StartY=78.0926 StartZ=0 EndX=-40.5 EndY=78.0926 EndZ=0
    g1: LineSegment StartX=-40.5 StartY=78.0926 StartZ=0 EndX=-40.5 EndY=70.0761 EndZ=0
    g2: LineSegment StartX=-40.5 StartY=70.0761 StartZ=0 EndX=-38.5 EndY=70.0761 EndZ=0
    g3: LineSegment StartX=-38.5 StartY=70.0761 StartZ=0 EndX=-38.5 EndY=78.0926 EndZ=0
  constraints (12):
    c: Coincident(g0,g1)
    c: Coincident(g1,g2)
    c: Coincident(g2,g3)
    c: Coincident(g3,g0)
    c: Horizontal(g0)
    c: Horizontal(g2)
    c: Vertical(g1)
    c: Vertical(g3)
    c: DistanceY(g-1,g2) = 70.0761
    c: DistanceY(g2,g0) = 8.01652
    c: DistanceX(g0,g0) = 2
    c: DistanceX(g2,g-1) = 38.5
FEATURE [PartDesign::Pocket] Pocket009  label="ventilSupFente"
  AllowMultiFace = false
  BaseFeature = -> LinearPattern001
  Direction = (0,0.707107,0.707107)
  Length = 5
  Length2 = 100
  Profile = -> Sketch015
  Reversed = true
  Type = 0
FEATURE [PartDesign::LinearPattern] LinearPattern002  label="ventilSupRepeat1"
  BaseFeature = -> Pocket009
  Direction = -> Sketch015 [H_Axis]
  Length = 28
  Occurrences = 8
  Originals = -> [Pocket009]
  Reversed = true
  expr: Length = <<sp>>.ventilLargeurRepet
  expr: Occurrences = <<sp>>.ventilNbrFents
FEATURE [PartDesign::LinearPattern] LinearPattern003  label="ventilSupRepeat2"
  BaseFeature = -> LinearPattern002
  Direction = -> Sketch015 [H_Axis]
  Length = 32
  Occurrences = 9
  Originals = -> [Pocket009]
  expr: Length = <<sp>>.ventilLargeurRepet + <<sp>>.ventilEcartfente + <<sp>>.ventilLargeurFentes
  expr: Occurrences = <<sp>>.ventilNbrFents + 1
FEATURE [PartDesign::Plane] DatumPlane007  label="planTrancheurBis"
  AttachmentOffset = pos=(0,0,71) rot=(-1,0,0;0.785398rad)
  Length = 123.775
  MapMode = 5
  Placement = pos=(0,-71,-1.58e-14) rot=(1,0,0;0.785398rad)
  ResizeMode = 0
  Support = -> [XZ_Plane003]
  Width = 165.093
  expr: .AttachmentOffset.Base.z = <<sp>>.planTrancheur
FEATURE [Sketcher::SketchObject] Sketch016  label="sk_insertFavDroit"
  FullyConstrained = true
  MapMode = 5
  Placement = pos=(0,-71,-2.13e-14) rot=(1,0,0;0.785398rad)
  Support = -> [DatumPlane007]
  expr: Constraints[11] = <<sp>>.insertFAVDistBord
  expr: Constraints[14] = <<sp>>.insertFAVDistBord / 2
  expr: Constraints[7] = <<sp>>.epaisseurParois
  expr: Constraints[8] = <<sp>>.insertFavDistAuZeroDuPLan + <<sp>>.epaisseurParois
  expr: Constraints[9] = <<sp>>.insertFAVDistBord
  sketch-geometry (5):
    g0: LineSegment StartX=-6.5 StartY=14.7426 StartZ=0 EndX=-2.5 EndY=14.7426 EndZ=0
    g1: LineSegment StartX=-2.5 StartY=14.7426 StartZ=0 EndX=-2.5 EndY=6.74264 EndZ=0
    g2: LineSegment StartX=-2.5 StartY=6.74264 StartZ=0 EndX=-10.5 EndY=6.74264 EndZ=0
    g3: LineSegment StartX=-10.5 StartY=6.74264 StartZ=0 EndX=-10.5 EndY=10.7426 EndZ=0
    g4: ArcOfCircle CenterX=-6.5 CenterY=10.7426 CenterZ=0 NormalX=0 NormalY=0 NormalZ=1 AngleXU=0 Radius=4 StartAngle=1.5708 EndAngle=3.14159
  constraints (15):
    c: Horizontal(g0)
    c: Coincident(g0,g1)
    c: Vertical(g1)
    c: Coincident(g1,g2)
    c: Horizontal(g2)
    c: Coincident(g2,g3)
    c: Vertical(g3)
    c: DistanceX(g1,g-1) = 2.5
    c: DistanceY(g-1,g1) = 6.74264
    c: DistanceY(g1,g1) = 8
    c: Equal(g3,g0)
    c: DistanceX(g2,g2) = 8
    c: Coincident(g4,g0)
    c: Tangent(g4,g3) = 1.5708
    c: DistanceX(g4,g1) = 4
FEATURE [PartDesign::Pad] Pad005  label="padInsertFavDroit"
  AllowMultiFace = false
  BaseFeature = -> Thickness001
  Direction = (0,-0.707107,0.707107)
  Length = 10
  Length2 = 100
  Profile = -> Sketch016
  Type = 2
FEATURE [Sketcher::SketchObject] Sketch017  label="sp_padInserFavGauch"
  FullyConstrained = true
  MapMode = 5
  Placement = pos=(0,-71,-2.13e-14) rot=(1,0,0;0.785398rad)
  Support = -> [DatumPlane007]
  expr: Constraints[10] = <<sp>>.insertFAVDistBord
  expr: Constraints[12] = <<sp>>.insertFAVDistBord / 2
  expr: Constraints[13] = <<sp>>.largeurModuleBase
  expr: Constraints[14] = <<sp>>.insertFavDistAuZeroDuPLan
  expr: Constraints[15] = <<sp>>.epaisseurParois
  expr: Constraints[16] = <<sp>>.epaisseurParois
  sketch-geometry (6):
    g0: LineSegment StartX=-68.5 StartY=14.7426 StartZ=0 EndX=-72.5 EndY=14.7426 EndZ=0
    g1: LineSegment StartX=-72.5 StartY=14.7426 StartZ=0 EndX=-72.5 EndY=6.74264 EndZ=0
    g2: LineSegment StartX=-72.5 StartY=6.74264 StartZ=0 EndX=-64.5 EndY=6.74264 EndZ=0
    g3: LineSegment StartX=-64.5 StartY=6.74264 StartZ=0 EndX=-64.5 EndY=10.7426 EndZ=0
    g4: ArcOfCircle CenterX=-68.5 CenterY=10.7426 CenterZ=0 NormalX=0 NormalY=0 NormalZ=1 AngleXU=0 Radius=4 StartAngle=-4.5377e-12 EndAngle=1.5708
    g5: GeomPoint X=-75 Y=4.24264 Z=0
  constraints (17):
    c: Horizontal(g0)
    c: Coincident(g0,g1)
    c: Vertical(g1)
    c: Coincident(g1,g2)
    c: Horizontal(g2)
    c: Coincident(g2,g3)
    c: Vertical(g3)
    c: Equal(g3,g0)
    c: Equal(g2,g1)
    c: Coincident(g0,g4)
    c: DistanceX(g2,g2) = 8
    c: Tangent(g4,g3) = -1.5708
    c: DistanceX(g0,g0) = 4
    c: DistanceX(g5,g-1) = 75
    c: DistanceY(g-1,g5) = 4.24264
    c: DistanceY(g5,g1) = 2.5
    c: DistanceX(g5,g1) = 2.5
FEATURE [PartDesign::Pad] Pad006  label="padInsertFavGauch"
  AllowMultiFace = false
  BaseFeature = -> Pad005
  Direction = (0,-0.707107,0.707107)
  Length = 10
  Length2 = 100
  Profile = -> Sketch017
  Type = 2
FEATURE [Sketcher::SketchObject] Sketch018  label="skPercageInsertFavDroit"
  FullyConstrained = true
  MapMode = 5
  Placement = pos=(0,-71,-2.13e-14) rot=(1,0,0;0.785398rad)
  Support = -> [DatumPlane007]
  expr: Constraints[0] = <<sp>>.insertDiamPercage
  expr: Constraints[1] = <<sp>>.insertFavDistAuZeroDuPLan + <<sp>>.epaisseurParois + <<sp>>.insertFAVDistBord / 2
  expr: Constraints[2] = <<sp>>.epaisseurParois + <<sp>>.insertFAVDistBord / 2
  expr: Constraints[7] = <<sp>>.largeurModuleBase - 2 * <<sp>>.epaisseurParois - <<sp>>.insertFAVDistBord
  sketch-geometry (3):
    g0: Circle CenterX=-6.5 CenterY=10.7426 CenterZ=0 NormalX=0 NormalY=0 NormalZ=1 AngleXU=0 Radius=2
    g1: Circle CenterX=-68.5 CenterY=10.7426 CenterZ=0 NormalX=0 NormalY=0 NormalZ=1 AngleXU=0 Radius=2
    g2: LineSegment StartX=-68.5 StartY=10.7426 StartZ=0 EndX=-6.5 EndY=10.7426 EndZ=0
  constraints (8):
    c: Diameter(g0) = 4
    c: DistanceY(g-1,g0) = 10.7426
    c: DistanceX(g0,g-1) = 6.5
    c: Equal(g0,g1)
    c: Coincident(g2,g1)
    c: Coincident(g2,g0)
    c: Horizontal(g2)
    c: DistanceX(g2,g2) = 62
FEATURE [PartDesign::Pocket] Pocket010  label="trouInsertFavDroit"
  AllowMultiFace = false
  BaseFeature = -> Pad006
  Direction = (0,0.707107,-0.707107)
  Length = 8
  Length2 = 100
  Profile = -> Sketch018
  Reversed = true
  Type = 0
  expr: Length = <<sp>>.insertFavProfondeur
FEATURE [PartDesign::Body] Body001  label="base"
  BaseFeature = -> Slice_child0
  Group = -> [Clone,Thickness,DatumPlane001,Sketch002,Pad001,Sketch003,Pocket,DatumPlane002,Sketch004,Pocket001,Sketch005,Pocket002,Sketch006,Pocket003,DatumPlane003,DatumPlane004,Sketch008,Pad003,Sketch009,Pad004,Sketch010,Pocket004,Sketch011,Pocket005,DatumPlane005,Sketch012,Pocket006,Sketch014,Pocket008,LinearPattern,LinearPattern001,DatumPlane006,Sketch015,Pocket009,LinearPattern002,LinearPattern003,+3 more]
  Origin = -> Origin002
  Tip = -> Pocket015
FEATURE [PartDesign::Plane] DatumPlane011  label="planFaceAvant"
  AttachmentOffset = pos=(0,0,93.2843) rot=(-1,0,0;0.785398rad)
  Length = 123.775
  MapMode = 5
  Placement = pos=(0,-93.2843,-2.07e-14) rot=(1,0,0;0.785398rad)
  ResizeMode = 0
  Support = -> [XZ_Plane003]
  Width = 165.093
  expr: .AttachmentOffset.Base.z = <<sp>>.planFaceAvant
FEATURE [Sketcher::SketchObject] Sketch030  label="sk_rebordFav"
  FullyConstrained = true
  MapMode = 5
  Placement = pos=(0,-71,-2.13e-14) rot=(1,0,0;0.785398rad)
  Support = -> [DatumPlane007]
  expr: Constraints[0] = <<sp>>.insertFavDistAuZeroDuPLan
  expr: Constraints[19] = <<sp>>.epaisseurParois
  expr: Constraints[20] = <<sp>>.favEpBordure
  expr: Constraints[21] = <<sp>>.favDistBordPlan
  expr: Constraints[22] = <<sp>>.largeurModuleBase - 2 * <<sp>>.epaisseurParois
  expr: Constraints[23] = <<sp>>.favEpBordure
  expr: Constraints[24] = <<sp>>.Face - <<sp>>.epaisseurParois
  expr: Constraints[25] = <<sp>>.favEpBordure
  sketch-geometry (9):
    g0: GeomPoint X=0 Y=4.24264 Z=0
    g1: LineSegment StartX=-72.5 StartY=20.9853 StartZ=0 EndX=-72.5 EndY=81.7426 EndZ=0
    g2: LineSegment StartX=-72.5 StartY=81.7426 StartZ=0 EndX=-2.5 EndY=81.7426 EndZ=0
    g3: LineSegment StartX=-2.5 StartY=81.7426 StartZ=0 EndX=-2.5 EndY=20.9853 EndZ=0
    g4: LineSegment StartX=-2.5 StartY=20.9853 StartZ=0 EndX=-4 EndY=20.9853 EndZ=0
    g5: LineSegment StartX=-4 StartY=20.9853 StartZ=0 EndX=-4 EndY=80.2426 EndZ=0
    g6: LineSegment StartX=-4 StartY=80.2426 StartZ=0 EndX=-71 EndY=80.2426 EndZ=0
    g7: LineSegment StartX=-71 StartY=80.2426 StartZ=0 EndX=-71 EndY=20.9853 EndZ=0
    g8: LineSegment StartX=-71 StartY=20.9853 StartZ=0 EndX=-72.5 EndY=20.9853 EndZ=0
  constraints (26):
    c: DistanceY(g-1,g0) = 4.24264
    c: Vertical(g0,g-1)
    c: Vertical(g1)
    c: Coincident(g1,g2)
    c: Horizontal(g2)
    c: Coincident(g2,g3)
    c: Vertical(g3)
    c: Coincident(g3,g4)
    c: Horizontal(g4)
    c: Coincident(g4,g5)
    c: Vertical(g5)
    c: Coincident(g5,g6)
    c: Horizontal(g6)
    c: Coincident(g6,g7)
    c: Vertical(g7)
    c: Coincident(g7,g8)
    c: Coincident(g8,g1)
    c: Horizontal(g8)
    c: Horizontal(g7,g4)
    c: DistanceX(g3,g0) = 2.5
    c: DistanceX(g4,g4) = 1.5
    c: DistanceY(g0,g3) = 16.7426
    c: DistanceX(g1,g3) = 70
    c: DistanceY(g5,g2) = 1.5
    c: DistanceY(g0,g2) = 77.5
    c: DistanceX(g1,g7) = 1.5
FEATURE [PartDesign::Pad] Pad014  label="favRebordSupport"
  AllowMultiFace = false
  BaseFeature = -> Pocket010
  Direction = (0,-0.707107,0.707107)
  Length = 10
  Length2 = 100
  Profile = -> Sketch030
  Type = 3
  UpToFace = -> Pocket010 [Face13]
FEATURE [PartDesign::Pad] Pad015  label="favRebord"
  AllowMultiFace = false
  BaseFeature = -> Pad014
  Direction = (0,-0.707107,0.707107)
  Length = 4.15
  Length2 = 100
  Profile = -> Sketch030
  Reversed = true
  Type = 0
  expr: Length = <<sp>>.favBordureProf
FEATURE [Sketcher::SketchObject] Sketch031  label="sk_bourlet"
  ExternalGeometry = -> [Pad015]
  FullyConstrained = true
  MapMode = 5
  Placement = pos=(-2.5,0,0) rot=(0.57735,0.57735,0.57735;2.0944rad)
  Support = -> [Pad015]
  expr: Constraints[3] = <<sp>>.bourletMaintientRayon - <<sp>>.bourletRayonJeu
  sketch-geometry (2):
    g0: ArcOfCircle CenterX=-11.184 CenterY=55.7855 CenterZ=0 NormalX=0 NormalY=0 NormalZ=1 AngleXU=0 Radius=1.3 StartAngle=5.49779 EndAngle=8.63938
    g1: LineSegment StartX=-12.1032 StartY=56.7048 StartZ=0 EndX=-10.2647 EndY=54.8663 EndZ=0
  constraints (6):
    c: Coincident(g0,g-3)
    c: PointOnObject(g0,g-3)
    c: PointOnObject(g0,g-3)
    c: Radius(g0) = 1.3
    c: Coincident(g1,g0)
    c: Coincident(g1,g0)
FEATURE [PartDesign::Pad] Pad016  label="bourlet"
  AllowMultiFace = false
  BaseFeature = -> Pad015
  Direction = (1,0,0)
  Length = 10
  Length2 = 100
  Profile = -> Sketch031
  Reversed = true
  Type = 3
  UpToFace = -> Pad015 [Face11]
FEATURE [Sketcher::SketchObject] Sketch039
  FullyConstrained = true
  MapMode = 5
  Placement = pos=(0,-93.2843,-2.84e-14) rot=(1,0,0;0.785398rad)
  Support = -> [DatumPlane011]
  expr: Constraints[15] = <<favTrousSp>>.trousDiam
  expr: Constraints[16] = <<favTrousSp>>.visEcartY
  expr: Constraints[17] = <<favTrousSp>>.visEcartX
  expr: Constraints[19] = <<favTrousSp>>.planAdap
  expr: Constraints[20] = <<favTrousSp>>.posAdapY
  sketch-geometry (9):
    g0: LineSegment StartX=-65.475 StartY=92 StartZ=0 EndX=-9.525 EndY=92 EndZ=0
    g1: LineSegment StartX=-9.525 StartY=92 StartZ=0 EndX=-9.525 EndY=46 EndZ=0
    g2: LineSegment StartX=-9.525 StartY=46 StartZ=0 EndX=-65.475 EndY=46 EndZ=0
    g3: LineSegment StartX=-65.475 StartY=46 StartZ=0 EndX=-65.475 EndY=92 EndZ=0
    g4: Circle CenterX=-65.475 CenterY=92 CenterZ=0 NormalX=0 NormalY=0 NormalZ=1 AngleXU=0 Radius=2
    g5: Circle CenterX=-9.525 CenterY=92 CenterZ=0 NormalX=0 NormalY=0 NormalZ=1 AngleXU=0 Radius=2
    g6: Circle CenterX=-65.475 CenterY=46 CenterZ=0 NormalX=0 NormalY=0 NormalZ=1 AngleXU=0 Radius=2
    g7: Circle CenterX=-9.525 CenterY=46 CenterZ=0 NormalX=0 NormalY=0 NormalZ=1 AngleXU=0 Radius=2
    g8: GeomPoint X=-37.5 Y=46 Z=0
  constraints (21):
    c: Coincident(g0,g1)
    c: Coincident(g1,g2)
    c: Coincident(g2,g3)
    c: Coincident(g3,g0)
    c: Horizontal(g0)
    c: Horizontal(g2)
    c: Vertical(g1)
    c: Vertical(g3)
    c: Coincident(g4,g0)
    c: Coincident(g5,g0)
    c: Coincident(g6,g2)
    c: Coincident(g7,g1)
    c: Equal(g4,g5)
    c: Equal(g5,g7)
    c: Equal(g7,g6)
    c: Diameter(g4) = 4
    c: DistanceY(g7,g5) = 46
    c: DistanceX(g6,g7) = 55.95
    c: Symmetric(g6,g7,g8)
    c: DistanceX(g8,g-1) = 37.5
    c: DistanceY(g-1,g7) = 46
FEATURE [PartDesign::Pocket] Pocket018  label="trouVisAdapt"
  BaseFeature = -> Pad016
  Direction = (0,0.707107,-0.707107)
  Length = 5
  Length2 = 5
  Profile = -> Sketch039
  ReferenceAxis = -> Sketch039 [N_Axis]
  Type = 1
FEATURE [Sketcher::SketchObject] Sketch040
  FullyConstrained = true
  MapMode = 5
  Placement = pos=(0,-93.2843,-2.84e-14) rot=(1,0,0;0.785398rad)
  Support = -> [DatumPlane011]
  expr: Constraints[12] = <<favTrousSp>>.planAdap
  expr: Constraints[8] = <<favTrousSp>>.passCableLarg
  expr: Constraints[9] = <<favTrousSp>>.passCableLong
  sketch-geometry (5):
    g0: LineSegment StartX=-47.5 StartY=68 StartZ=0 EndX=-27.5 EndY=68 EndZ=0
    g1: LineSegment StartX=-27.5 StartY=68 StartZ=0 EndX=-27.5 EndY=41.2 EndZ=0
    g2: LineSegment StartX=-27.5 StartY=41.2 StartZ=0 EndX=-47.5 EndY=41.2 EndZ=0
    g3: LineSegment StartX=-47.5 StartY=41.2 StartZ=0 EndX=-47.5 EndY=68 EndZ=0
    g4: GeomPoint X=-37.5 Y=41.2 Z=0
  constraints (13):
    c: Coincident(g0,g1)
    c: Coincident(g1,g2)
    c: Coincident(g2,g3)
    c: Coincident(g3,g0)
    c: Horizontal(g0)
    c: Horizontal(g2)
    c: Vertical(g1)
    c: Vertical(g3)
    c: DistanceX(g2,g1) = 20
    c: DistanceY(g1,g0) = 26.8
    c: DistanceY(g-1,g1) = 41.2
    c: Symmetric(g2,g1,g4)
    c: DistanceX(g4,g-1) = 37.5
FEATURE [PartDesign::Pocket] Pocket019  label="passageCable"
  BaseFeature = -> Pocket018
  Direction = (0,0.707107,-0.707107)
  Length = 5
  Length2 = 5
  Profile = -> Sketch040
  ReferenceAxis = -> Sketch040 [N_Axis]
  Type = 1
FEATURE [PartDesign::Body] Body002  label="faceAvant"
  BaseFeature = -> Slice_child1
  Group = -> [Clone001,Thickness001,DatumPlane007,Sketch016,Pad005,Sketch017,Pad006,Sketch018,Pocket010,DatumPlane011,Sketch030,Pad014,Pad015,Sketch031,Pad016,Sketch039,Pocket018,Sketch040,Pocket019]
  Origin = -> Origin003
  Tip = -> Pocket019
COMPONENT P7 — geometry summary ("visInsertsAdapt"; no construction recipe available for this part):
  bounding box: 61.5 x 42.0 x 41.9 mm
  tessellated surface: 4,112 triangles
  volume: 368 mm^3 (0% of its bounding box)
  symmetry: mirror-symmetric across its x mid-plane
PROVENANCE & LICENSES
A FreeCAD (.FCStd) document from a public repository crawl; recipes are the document's own serialized feature recipes (and, for linked parts, companion documents' recipes).
License: as declared in the source repository (recorded in the dataset sidecar).
